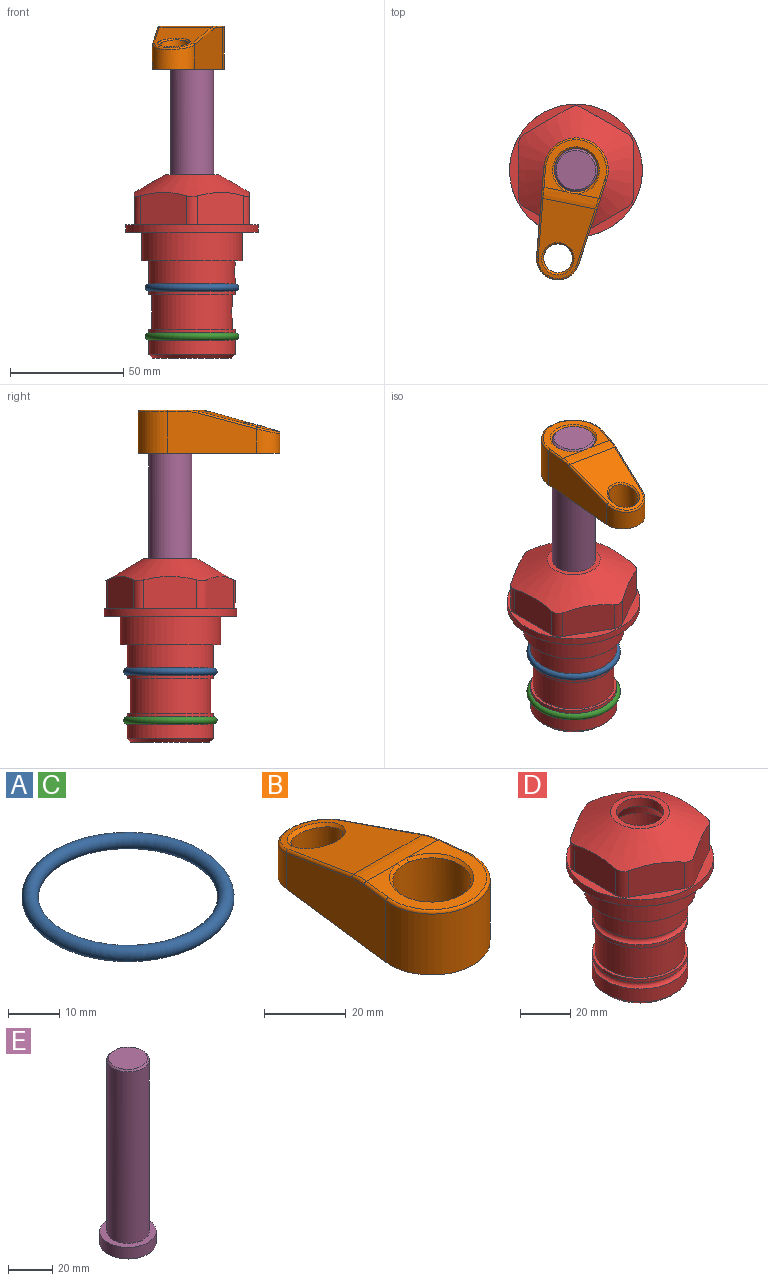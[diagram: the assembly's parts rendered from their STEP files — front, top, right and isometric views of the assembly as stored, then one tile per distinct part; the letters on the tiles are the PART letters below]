
ASSEMBLY  parts=5 mates=4
PART A: 1 faces, bbox 44.7x44.7x3.2 mm
  f0: torus R=19.05mm, axis (0,0,1), area 1193.9mm2
PART B: 31 faces, bbox 31.7x65.5x19.8 mm
  f0: plane 39.12x18.26mm, normal (0.99,0.12,0), area 612.2mm2, adj f1,f4,f7,f11,f13,f15
  f1: cylinder r=9.53mm len=18.91mm, axis (0,0,-1), area 296.1mm2, adj f0,f2,f7,f17
  f2: plane 39.12x18.26mm, normal (-0.99,0.12,0), area 612.2mm2, adj f1,f4,f7,f12,f14,f16
  f3: cylinder r=6.35mm len=12.7mm, axis (0,0,-1), area 362.4mm2, adj f7,f18
  f4: cylinder r=14.29mm len=28.58mm, axis (0,0,-1), area 882.2mm2, adj f0,f2,f7,f10
  f5: cylinder r=9.53mm len=19.05mm, axis (0,0,-1), area 1092.6mm2, adj f7,f19,f20
  f6: plane 26.99x23.69mm, normal (0,0,1), area 216.2mm2, adj f9,f10,f11,f12,f19
  f7: plane 63.5x28.58mm, normal (0,0,-1), area 661.8mm2, adj f0,f1,f2,f3,f4,f5,f22,f23
  f8: plane 33.52x23.6mm, normal (0,0.26,0.97), area 486mm2, adj f9,f15,f16,f17,f18
  f9: cylinder r=19.05mm len=24.72mm, axis (1,0,0), area 120.4mm2, adj f6,f8,f13,f14,f20
  f10: torus R=13.49mm, axis (0,0,1), area 59mm2, adj f4,f6,f11,f12
  f11: cylinder r=0.79mm len=8.67mm, axis (0.12,-0.99,0), area 10.8mm2, adj f0,f6,f10,f13
  f12: cylinder r=0.79mm len=8.67mm, axis (0.12,0.99,0), area 10.8mm2, adj f2,f6,f10,f14
  f13: bspline ~4.95x1.42mm, area 6.1mm2, adj f0,f9,f11,f15
  f14: bspline ~4.95x1.42mm, area 6.1mm2, adj f2,f9,f12,f16
  f15: cylinder r=0.79mm len=25.95mm, axis (0.12,-0.96,0.26), area 32.9mm2, adj f0,f8,f13,f17
  f16: cylinder r=0.79mm len=25.95mm, axis (0.12,0.96,-0.26), area 32.9mm2, adj f2,f8,f14,f17
  f17: bspline ~18.91x8.38mm, area 30mm2, adj f1,f8,f15,f16
  f18: bspline ~14.29x14.29mm, area 48.3mm2, adj f3,f8
  f19: cone r=9.53mm half-angle=45deg, axis (0,0,1), area 66.5mm2, adj f5,f6,f20
  f20: bspline ~3.22x0.96mm, area 3.5mm2, adj f5,f9,f19
  f21: plane 2.75x2.72mm, normal (0,0,-1), area 2.9mm2, adj f23,f25,f28
  f22: plane 23.05x15.88mm, normal (-0.99,-0.12,0), area 323.6mm2, adj f7,f25,f26,f27,f28,f29
  f23: plane 23.05x15.88mm, normal (0.99,-0.12,0), area 323.6mm2, adj f7,f21,f25,f27,f28,f30
  f24: cylinder r=9.53mm len=10.69mm, axis (0,0,-1), area 114.7mm2, adj f7,f27,f29,f30
  f25: cylinder r=12.7mm len=20.59mm, axis (0,0,-1), area 381.1mm2, adj f7,f21,f22,f23,f26,f28
  f26: plane 2.75x2.72mm, normal (0,0,-1), area 2.9mm2, adj f22,f25,f28
  f27: plane 19.72x18.37mm, normal (0,-0.26,-0.97), area 291.8mm2, adj f22,f23,f24,f28,f29,f30
  f28: cylinder r=15.88mm len=19.92mm, axis (1,0,0), area 54.8mm2, adj f21,f22,f23,f25,f26,f27
  f29: cylinder r=1.59mm len=11mm, axis (0,0,-1), area 34.7mm2, adj f7,f22,f24,f27
  f30: cylinder r=1.59mm len=11mm, axis (0,0,-1), area 34.7mm2, adj f7,f23,f24,f27
PART C: same geometry as A
PART D: 36 faces, bbox 58.7x58.7x81 mm
  f0: cylinder r=17.78mm len=35.56mm, axis (0,0,1), area 1670.8mm2, adj f23,f24,f31
  f1: cylinder r=19.05mm len=38.1mm, axis (0,0,1), area 1191.9mm2, adj f26,f27,f30
  f2: plane 58.66x58.66mm, normal (0,0,-1), area 1150.6mm2, adj f3,f28
  f3: cylinder r=29.33mm len=58.66mm, axis (0,0,-1), area 585.1mm2, adj f2,f4
  f4: plane 58.66x58.66mm, normal (0,0,1), area 475.9mm2, adj f3,f5,f6,f7,f8,f9,f10,f11
  f5: plane 20.32x14.34mm, normal (-0.5,0.87,0), area 324.4mm2, adj f4,f15,f16,f17
  f6: plane 20.32x14.34mm, normal (0.5,0.87,0), area 324.4mm2, adj f4,f14,f15,f17
  f7: plane 23.48x14.34mm, normal (1,0,0), area 324.4mm2, adj f4,f13,f14,f17
  f8: plane 20.32x14.34mm, normal (0.5,-0.87,0), area 324.4mm2, adj f4,f12,f13,f17
  f9: plane 20.32x14.34mm, normal (-0.5,-0.87,0), area 324.4mm2, adj f4,f11,f12,f17
  f10: plane 23.48x14.34mm, normal (-1,0,0), area 324.4mm2, adj f4,f11,f16,f17
  f11: cylinder r=5.08mm len=12.85mm, axis (0,0,-1), area 67.2mm2, adj f4,f9,f10,f17
  f12: cylinder r=5.08mm len=12.85mm, axis (0,0,-1), area 67.2mm2, adj f4,f8,f9,f17
  f13: cylinder r=5.08mm len=12.85mm, axis (0,0,-1), area 67.2mm2, adj f4,f7,f8,f17
  f14: cylinder r=5.08mm len=12.85mm, axis (0,0,-1), area 67.2mm2, adj f4,f6,f7,f17
  f15: cylinder r=5.08mm len=12.85mm, axis (0,0,-1), area 67.2mm2, adj f4,f5,f6,f17
  f16: cylinder r=5.08mm len=12.85mm, axis (0,0,-1), area 67.2mm2, adj f4,f5,f10,f17
  f17: cone r=11.73mm half-angle=60deg, axis (0,0,-1), area 2071.8mm2, adj f5,f6,f7,f8,f9,f10,f11,f12
  f18: plane 23.46x23.46mm, normal (0,0,1), area 147.4mm2, adj f17,f35
  f19: plane 34.93x34.93mm, normal (0,0,-1), area 958mm2, adj f29
  f20: cylinder r=19.05mm len=38.1mm, axis (0,0,1), area 760.1mm2, adj f21,f29
  f21: torus R=19.05mm, axis (0,0,1), area 565.3mm2, adj f20,f22
  f22: cylinder r=19.05mm len=38.1mm, axis (0,0,1), area 190mm2, adj f21,f23
  f23: plane 38.1x38.1mm, normal (0,0,1), area 146.9mm2, adj f0,f22
  f24: plane 38.1x38.1mm, normal (0,0,-1), area 146.9mm2, adj f0,f25
  f25: cylinder r=19.05mm len=38.1mm, axis (0,0,1), area 190mm2, adj f24,f26
  f26: torus R=19.05mm, axis (0,0,1), area 565.3mm2, adj f1,f25
  f27: plane 44.45x44.45mm, normal (0,0,-1), area 411.7mm2, adj f1,f28
  f28: cylinder r=22.23mm len=44.45mm, axis (0,0,1), area 1773.5mm2, adj f2,f27
  f29: cone r=19.05mm half-angle=45deg, axis (0,0,1), area 257.5mm2, adj f19,f20
  f30: cylinder r=3.17mm len=6.75mm, axis (-1,0,0), area 128mm2, adj f1,f33
  f31: cylinder r=3.17mm len=6.35mm, axis (-1,0,0), area 102.5mm2, adj f0,f33
  f32: plane 25.4x25.4mm, normal (0,0,1), area 506.7mm2, adj f33
  f33: cylinder r=12.7mm len=66.42mm, axis (0,0,-1), area 5236.2mm2, adj f30,f31,f32,f34
  f34: cone r=9.53mm half-angle=30deg, axis (0,0,-1), area 443.4mm2, adj f33,f35
  f35: cylinder r=9.53mm len=19.05mm, axis (0,0,-1), area 240.9mm2, adj f18,f34
PART E: 6 faces, bbox 25.4x25.4x101.6 mm
  f0: plane 17.46x17.46mm, normal (0,0,1), area 239.5mm2, adj f5
  f1: plane 25.4x25.4mm, normal (0,0,-1), area 506.7mm2, adj f2
  f2: cylinder r=12.7mm len=25.4mm, axis (0,0,1), area 506.7mm2, adj f1,f3
  f3: plane 25.4x25.4mm, normal (0,0,1), area 221.7mm2, adj f2,f4
  f4: cylinder r=9.53mm len=94.46mm, axis (0,0,1), area 5653mm2, adj f3,f5
  f5: cone r=8.73mm half-angle=45deg, axis (0,0,-1), area 64.4mm2, adj f0,f4
PLACE A at identity
PLACE B rot(axis=(0,0,1),168.5deg) t=(0,0,27.55)mm
PLACE C t=(0,0,-21.59)mm
PLACE D at identity fixed
PLACE E rot(axis=(0,0,1),168.5deg) t=(0,0,27.55)mm
MATE fastened C.f0 <-> D.f0  axis (0,0,1) through (0,0,-46.1)mm
MATE fastened A.f0 <-> D.f0  axis (0,0,1) through (0,0,-24.51)mm
MATE cylindrical E.f2 <-> D.f0  axis (0,0,-1) through (0,0,-10.55)mm
MATE fastened E.f2 <-> B.f4  axis (0,0,1) through (0,0,91.05)mm
